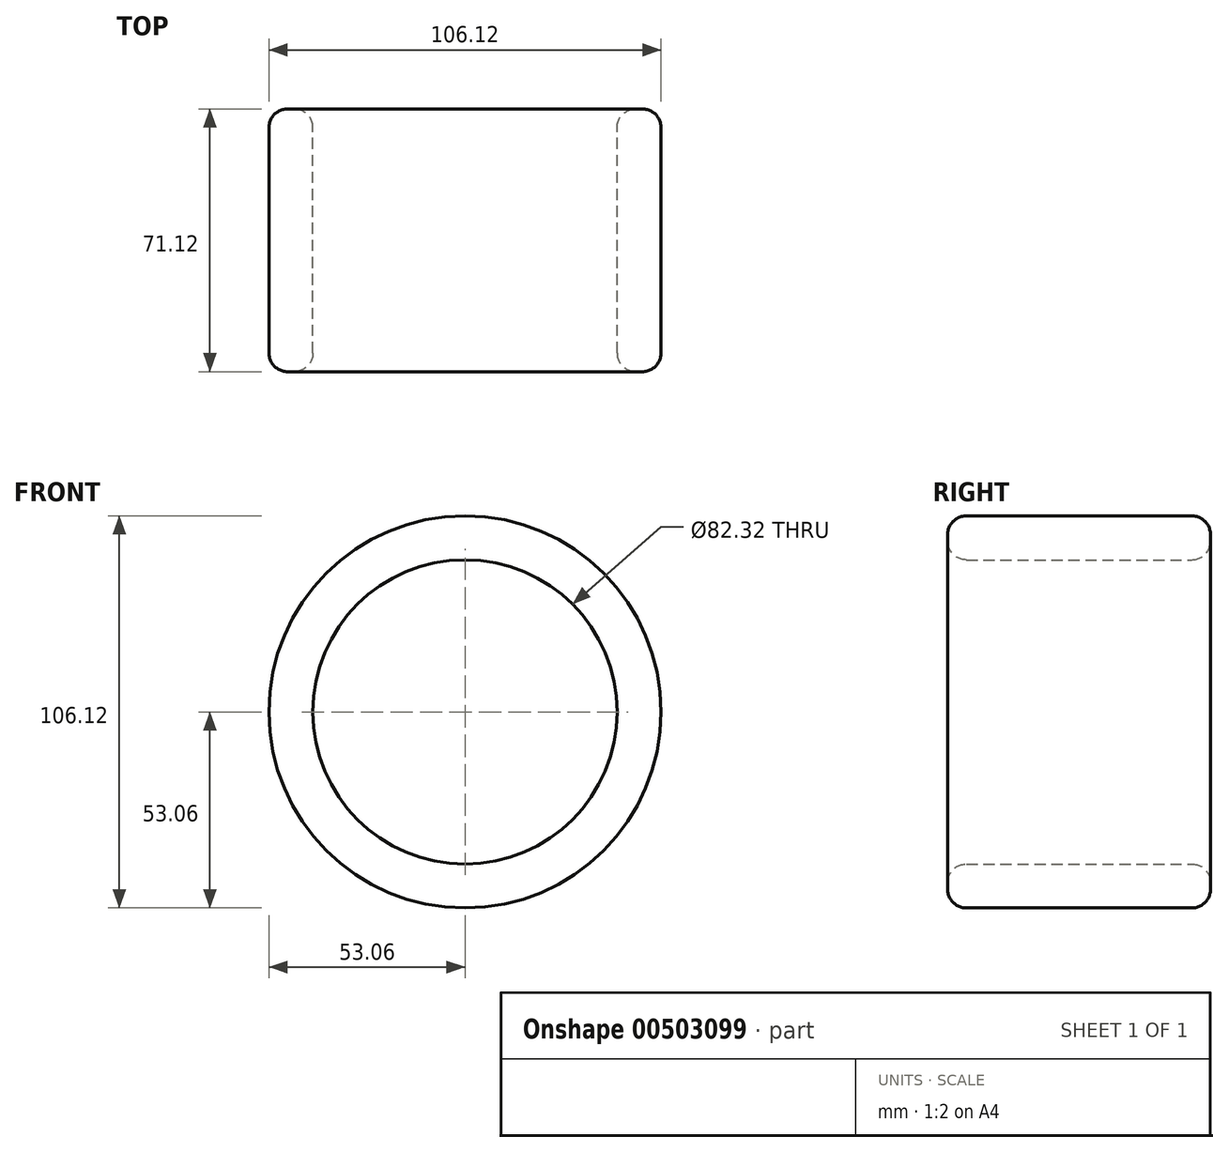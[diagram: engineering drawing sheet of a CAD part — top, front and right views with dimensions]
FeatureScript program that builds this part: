
annotation { "Feature Type Name" : "Feature", "Feature Type Description" : "" }
export const myFeature = defineFeature(function(context is Context, id is Id, definition is map)
    precondition{}
    {
        {
            var Q0;
            Q0=qCreatedBy(makeId("Front.planeOp"),FACE);
            var sketch = newSketch(context, id + "F0", { "sketchPlane" : qUnion([Q0])});
            skCircle(sketch, "E0", {"center": v(0, 0) * mm, "radius": 53.06 * mm});
            skCircle(sketch, "E1", {"center": v(0, 0) * mm, "radius": 41.16 * mm});
            skSolve(sketch);
        }
        {
            var Q0;
            Q0 = qSketchRegion(id + "F0", true);
            extrude(context, id + "F1", {"entities" : qUnion([Q0]), "depth" : 71.12 * mm});
        }
        {
            var Q0;
            Q0=makeQuery(id+"F1.opExtrude","CAP_EDGE",EDGE,{"disambiguationData":[OSD([sQuery(id+"F0.wireOp",EDGE,"E0")])],"isStart":false});
            fillet(context, id + "F2", {"entities" : qUnion([Q0]), "radius" : 5.08 * mm, "tangentPropagation" : true, "allowEdgeOverflow" : false});
        }
        {
            var Q0;
            Q0=makeQuery(id+"F1.opExtrude","CAP_EDGE",EDGE,{"disambiguationData":[OSD([sQuery(id+"F0.wireOp",EDGE,"E1")])],"isStart":false});
            fillet(context, id + "F3", {"entities" : qUnion([Q0]), "radius" : 5.08 * mm, "tangentPropagation" : true, "allowEdgeOverflow" : false});
        }
        {
            var Q0;
            Q0=makeQuery(id+"F1.opExtrude","CAP_EDGE",EDGE,{"disambiguationData":[OSD([sQuery(id+"F0.wireOp",EDGE,"E0")])],"isStart":true});
            fillet(context, id + "F4", {"entities" : qUnion([Q0]), "radius" : 5.08 * mm, "tangentPropagation" : true, "allowEdgeOverflow" : false});
        }
        {
            var Q0;
            Q0=makeQuery(id+"F1.opExtrude","CAP_EDGE",EDGE,{"disambiguationData":[OSD([sQuery(id+"F0.wireOp",EDGE,"E1")])],"isStart":true});
            fillet(context, id + "F5", {"entities" : qUnion([Q0]), "radius" : 5.08 * mm, "tangentPropagation" : true, "allowEdgeOverflow" : false});
        }
    });
